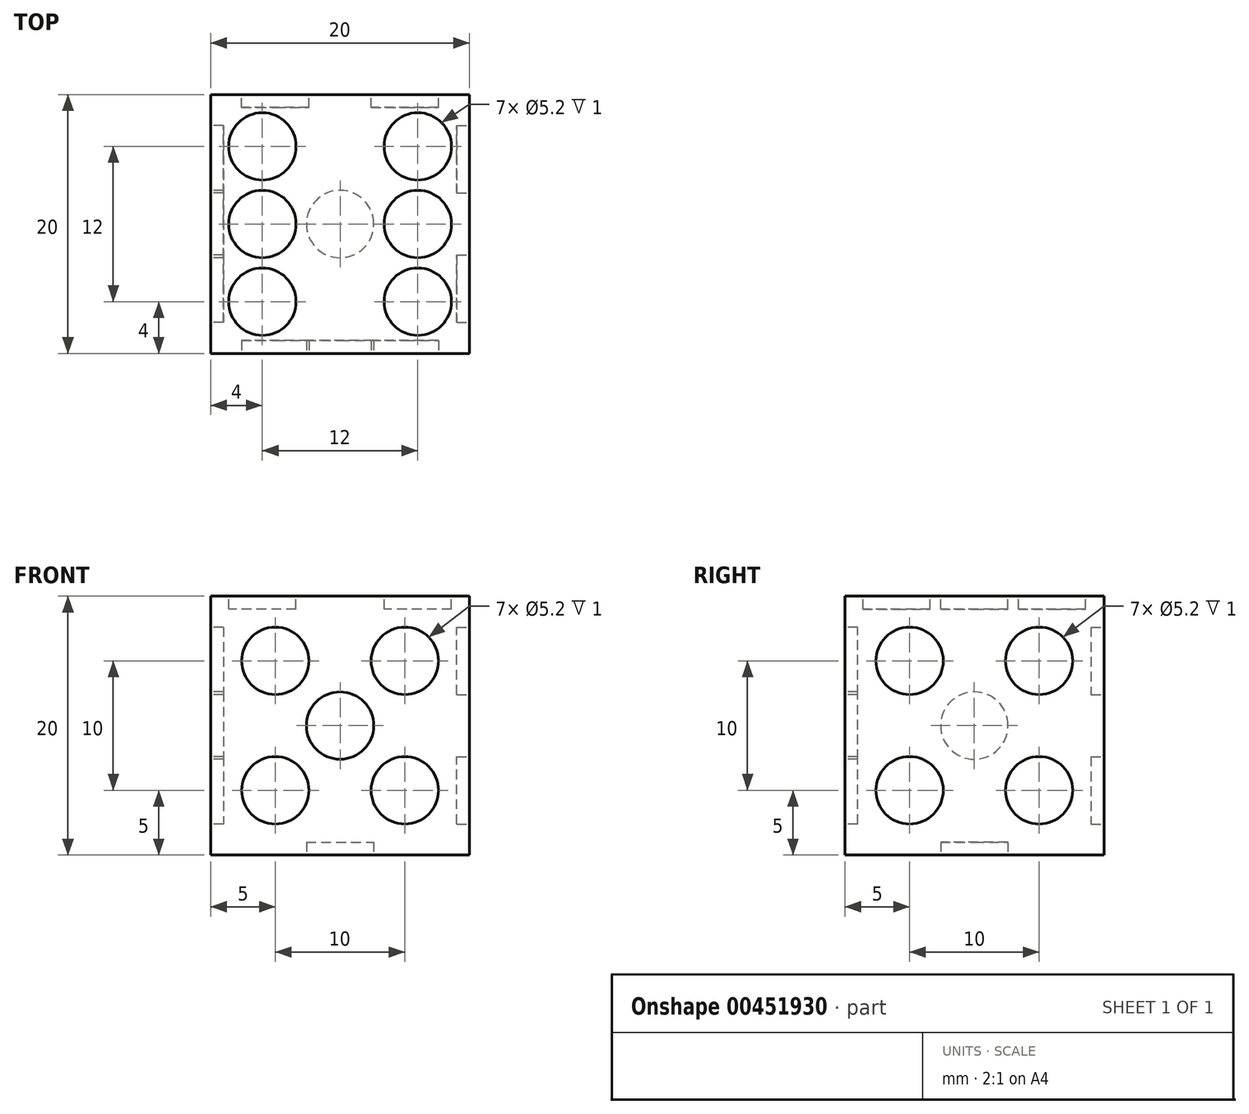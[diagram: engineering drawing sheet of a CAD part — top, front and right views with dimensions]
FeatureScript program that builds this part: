
annotation { "Feature Type Name" : "Feature", "Feature Type Description" : "" }
export const myFeature = defineFeature(function(context is Context, id is Id, definition is map)
    precondition{}
    {
        {
            var Q0;
            Q0=qCreatedBy(makeId("Front.planeOp"),FACE);
            var sketch = newSketch(context, id + "F0", { "sketchPlane" : qUnion([Q0])});
            skLineSegment(sketch, "E0.bottom", {"start": v(0, 0) * mm, "end": v(20, 0) * mm});
            skLineSegment(sketch, "E0.top", {"start": v(0, 20) * mm, "end": v(20, 20) * mm});
            skLineSegment(sketch, "E0.left", {"start": v(0, 0) * mm, "end": v(0, 20) * mm});
            skLineSegment(sketch, "E0.right", {"start": v(20, 0) * mm, "end": v(20, 20) * mm});
            skSolve(sketch);
        }
        {
            var Q0;
            Q0 = qSketchRegion(id + "F0", true);
            extrude(context, id + "F1", {"entities" : qUnion([Q0]), "depth" : 20 * mm});
        }
        {
            var Q0;
            Q0=makeQuery(id+"F1.opExtrude","CAP_FACE",FACE,{"disambiguationData":[OSD([sQuery(id+"F0.wireOp",EDGE,"E0.bottom"),sQuery(id+"F0.wireOp",EDGE,"E0.top"),sQuery(id+"F0.wireOp",EDGE,"E0.left"),sQuery(id+"F0.wireOp",EDGE,"E0.right")])],"isStart":false});
            var sketch = newSketch(context, id + "F2", { "sketchPlane" : qUnion([Q0])});
            skLineSegment(sketch, "E1", {"start": v(0, 20) * mm, "end": v(20, 0) * mm, "construction": true});
            skLineSegment(sketch, "E2", {"start": v(0, 0) * mm, "end": v(20, 20) * mm, "construction": true});
            skLineSegment(sketch, "E3", {"start": v(10, 20) * mm, "end": v(10, 0) * mm, "construction": true});
            skLineSegment(sketch, "E4", {"start": v(0, 10) * mm, "end": v(20, 10) * mm, "construction": true});
            skCircle(sketch, "E5", {"center": v(10, 10) * mm, "radius": 2.6 * mm});
            skCircle(sketch, "E6", {"center": v(5, 15) * mm, "radius": 2.6 * mm});
            skCircle(sketch, "E7.MirrorC", {"center": v(15, 15) * mm, "radius": 2.6 * mm});
            skCircle(sketch, "E8.MirrorC", {"center": v(15, 5) * mm, "radius": 2.6 * mm});
            skCircle(sketch, "E9.MirrorC", {"center": v(5, 5) * mm, "radius": 2.6 * mm});
            skSolve(sketch);
        }
        {
            var Q0;
            Q0 = qSketchRegion(id + "F2", true);
            extrude(context, id + "F3", {"entities" : qUnion([Q0]), "operationType" : NewBodyOperationType.REMOVE, "oppositeDirection" : true, "depth" : 1 * mm});
        }
        {
            var Q0;
            Q0=makeQuery(id+"F1.opExtrude","CAP_FACE",FACE,{"disambiguationData":[OSD([sQuery(id+"F0.wireOp",EDGE,"E0.bottom"),sQuery(id+"F0.wireOp",EDGE,"E0.top"),sQuery(id+"F0.wireOp",EDGE,"E0.left"),sQuery(id+"F0.wireOp",EDGE,"E0.right")])],"isStart":true});
            var sketch = newSketch(context, id + "F4", { "sketchPlane" : qUnion([Q0])});
            skLineSegment(sketch, "E10", {"start": v(-20, 0) * mm, "end": v(0, 20) * mm, "construction": true});
            skLineSegment(sketch, "E11", {"start": v(-20, 20) * mm, "end": v(0, 0) * mm, "construction": true});
            skLineSegment(sketch, "E12", {"start": v(-10, 20) * mm, "end": v(-10, 0) * mm, "construction": true});
            skLineSegment(sketch, "E13", {"start": v(-20, 10) * mm, "end": v(0, 10) * mm, "construction": true});
            skCircle(sketch, "E14", {"center": v(-5, 15) * mm, "radius": 2.6 * mm});
            skCircle(sketch, "E15.MirrorC", {"center": v(-15, 5) * mm, "radius": 2.6 * mm});
            skSolve(sketch);
        }
        {
            var Q0;
            Q0 = qSketchRegion(id + "F4", true);
            extrude(context, id + "F5", {"entities" : qUnion([Q0]), "operationType" : NewBodyOperationType.REMOVE, "oppositeDirection" : true, "depth" : 1 * mm});
        }
        {
            var Q0;
            Q0=makeQuery(id+"F1.opExtrude","SWEPT_FACE",FACE,{"disambiguationData":[OSD([sQuery(id+"F0.wireOp",EDGE,"E0.left")])]});
            var sketch = newSketch(context, id + "F6", { "sketchPlane" : qUnion([Q0])});
            skLineSegment(sketch, "E16", {"start": v(20, 20) * mm, "end": v(0, 0) * mm, "construction": true});
            skLineSegment(sketch, "E17", {"start": v(0, 20) * mm, "end": v(20, 0) * mm, "construction": true});
            skLineSegment(sketch, "E18", {"start": v(20, 10) * mm, "end": v(0, 10) * mm, "construction": true});
            skLineSegment(sketch, "E19", {"start": v(10, 20) * mm, "end": v(10, 0) * mm, "construction": true});
            skCircle(sketch, "E20", {"center": v(10, 10) * mm, "radius": 2.6 * mm});
            skCircle(sketch, "E21", {"center": v(15, 15) * mm, "radius": 2.6 * mm});
            skCircle(sketch, "E22.MirrorC", {"center": v(5, 5) * mm, "radius": 2.6 * mm});
            skSolve(sketch);
        }
        {
            var Q0;
            Q0 = qSketchRegion(id + "F6", true);
            extrude(context, id + "F7", {"entities" : qUnion([Q0]), "operationType" : NewBodyOperationType.REMOVE, "oppositeDirection" : true, "depth" : 1 * mm});
        }
        {
            var Q0;
            Q0=makeQuery(id+"F1.opExtrude","SWEPT_FACE",FACE,{"disambiguationData":[OSD([sQuery(id+"F0.wireOp",EDGE,"E0.right")])]});
            var sketch = newSketch(context, id + "F8", { "sketchPlane" : qUnion([Q0])});
            skLineSegment(sketch, "E23", {"start": v(0, 0) * mm, "end": v(-20, 20) * mm, "construction": true});
            skLineSegment(sketch, "E24", {"start": v(-20, 0) * mm, "end": v(0, 20) * mm, "construction": true});
            skLineSegment(sketch, "E25", {"start": v(-20, 10) * mm, "end": v(0, 10) * mm, "construction": true});
            skLineSegment(sketch, "E26", {"start": v(-10, 0) * mm, "end": v(-10, 20.9) * mm, "construction": true});
            skPoint(sketch, "E26.endSnap0", {"position": v(-10, 20) * mm});
            skCircle(sketch, "E27", {"center": v(-15, 5) * mm, "radius": 2.6 * mm});
            skCircle(sketch, "E28.MirrorC", {"center": v(-15, 15) * mm, "radius": 2.6 * mm});
            skLineSegment(sketch, "E29.MirrorCS", {"start": v(-10, 20) * mm, "end": v(-10, -0.9) * mm, "construction": true});
            skCircle(sketch, "E30.MirrorC", {"center": v(-5, 15) * mm, "radius": 2.6 * mm});
            skCircle(sketch, "E31.MirrorC", {"center": v(-5, 5) * mm, "radius": 2.6 * mm});
            skPoint(sketch, "E32.center.orphan", {"position": v(-10, 10) * mm});
            skSolve(sketch);
        }
        {
            var Q0;
            Q0 = qSketchRegion(id + "F8", true);
            extrude(context, id + "F9", {"entities" : qUnion([Q0]), "operationType" : NewBodyOperationType.REMOVE, "oppositeDirection" : true, "depth" : 1 * mm});
        }
        {
            var Q0;
            Q0=makeQuery(id+"F1.opExtrude","SWEPT_FACE",FACE,{"disambiguationData":[OSD([sQuery(id+"F0.wireOp",EDGE,"E0.bottom")])]});
            var sketch = newSketch(context, id + "F10", { "sketchPlane" : qUnion([Q0])});
            skLineSegment(sketch, "E33", {"start": v(0, 20) * mm, "end": v(20, 0) * mm, "construction": true});
            skLineSegment(sketch, "E34", {"start": v(20, 20) * mm, "end": v(0, 0) * mm, "construction": true});
            skLineSegment(sketch, "E35", {"start": v(10, 20) * mm, "end": v(10, 0) * mm, "construction": true});
            skLineSegment(sketch, "E36", {"start": v(0, 10) * mm, "end": v(20, 10) * mm, "construction": true});
            skCircle(sketch, "E37", {"center": v(10, 10) * mm, "radius": 2.6 * mm});
            skSolve(sketch);
        }
        {
            var Q0;
            Q0 = qSketchRegion(id + "F10", true);
            extrude(context, id + "F11", {"entities" : qUnion([Q0]), "operationType" : NewBodyOperationType.REMOVE, "oppositeDirection" : true, "depth" : 1 * mm});
        }
        {
            var Q0;
            Q0=makeQuery(id+"F1.opExtrude","SWEPT_FACE",FACE,{"disambiguationData":[OSD([sQuery(id+"F0.wireOp",EDGE,"E0.top")])]});
            var sketch = newSketch(context, id + "F12", { "sketchPlane" : qUnion([Q0])});
            skLineSegment(sketch, "E38", {"start": v(0, 0) * mm, "end": v(20, -20) * mm, "construction": true});
            skLineSegment(sketch, "E39", {"start": v(20, 0) * mm, "end": v(0, -20) * mm, "construction": true});
            skLineSegment(sketch, "E40", {"start": v(0, -10) * mm, "end": v(1.4, -10) * mm, "construction": true});
            skLineSegment(sketch, "E41", {"start": v(0, -16) * mm, "end": v(1.4, -16) * mm});
            skLineSegment(sketch, "E42", {"start": v(4, 0) * mm, "end": v(4, -1.4) * mm});
            skLineSegment(sketch, "E43", {"start": v(16, 0) * mm, "end": v(16, -1.4) * mm});
            skCircle(sketch, "E44", {"center": v(4, -4) * mm, "radius": 2.6 * mm});
            skCircle(sketch, "E45", {"center": v(4, -16) * mm, "radius": 2.6 * mm});
            skCircle(sketch, "E46", {"center": v(16, -16) * mm, "radius": 2.6 * mm});
            skCircle(sketch, "E47", {"center": v(4, -10) * mm, "radius": 2.6 * mm});
            skCircle(sketch, "E48", {"center": v(16, -4) * mm, "radius": 2.6 * mm});
            skLineSegment(sketch, "E49.trimOffspring", {"start": v(13.4, -4) * mm, "end": v(20, -4) * mm});
            skPoint(sketch, "E50.trimOffspring.end.orphan", {"position": v(20, -10) * mm});
            skPoint(sketch, "E51.start.orphan", {"position": v(10, 0) * mm});
            skPoint(sketch, "E52.trimOffspring.end.orphan", {"position": v(10, -20) * mm});
            skLineSegment(sketch, "E53.trimOffspring", {"start": v(13.4, -16) * mm, "end": v(18.6, -16) * mm});
            skPoint(sketch, "E54.center.orphan", {"position": v(16, -10) * mm});
            skCircle(sketch, "E55", {"center": v(16, -10) * mm, "radius": 2.6 * mm});
            skPoint(sketch, "E56.trimOffspring.end.orphan", {"position": v(16, -20) * mm});
            skLineSegment(sketch, "E57.trimOffspring", {"start": v(16, -12.6) * mm, "end": v(16, -13.4) * mm});
            skLineSegment(sketch, "E58.trimOffspring", {"start": v(16, -6.6) * mm, "end": v(16, -7.4) * mm});
            skPoint(sketch, "E59.orphan", {"position": v(4, -20) * mm});
            skLineSegment(sketch, "E60.trimOffspring", {"start": v(4, -12.6) * mm, "end": v(4, -13.4) * mm});
            skLineSegment(sketch, "E61.trimOffspring", {"start": v(4, -6.6) * mm, "end": v(4, -7.4) * mm});
            skSolve(sketch);
        }
        {
            var Q0;
            Q0 = qSketchRegion(id + "F12", true);
            extrude(context, id + "F13", {"entities" : qUnion([Q0]), "operationType" : NewBodyOperationType.REMOVE, "oppositeDirection" : true, "depth" : 1 * mm});
        }
    });
